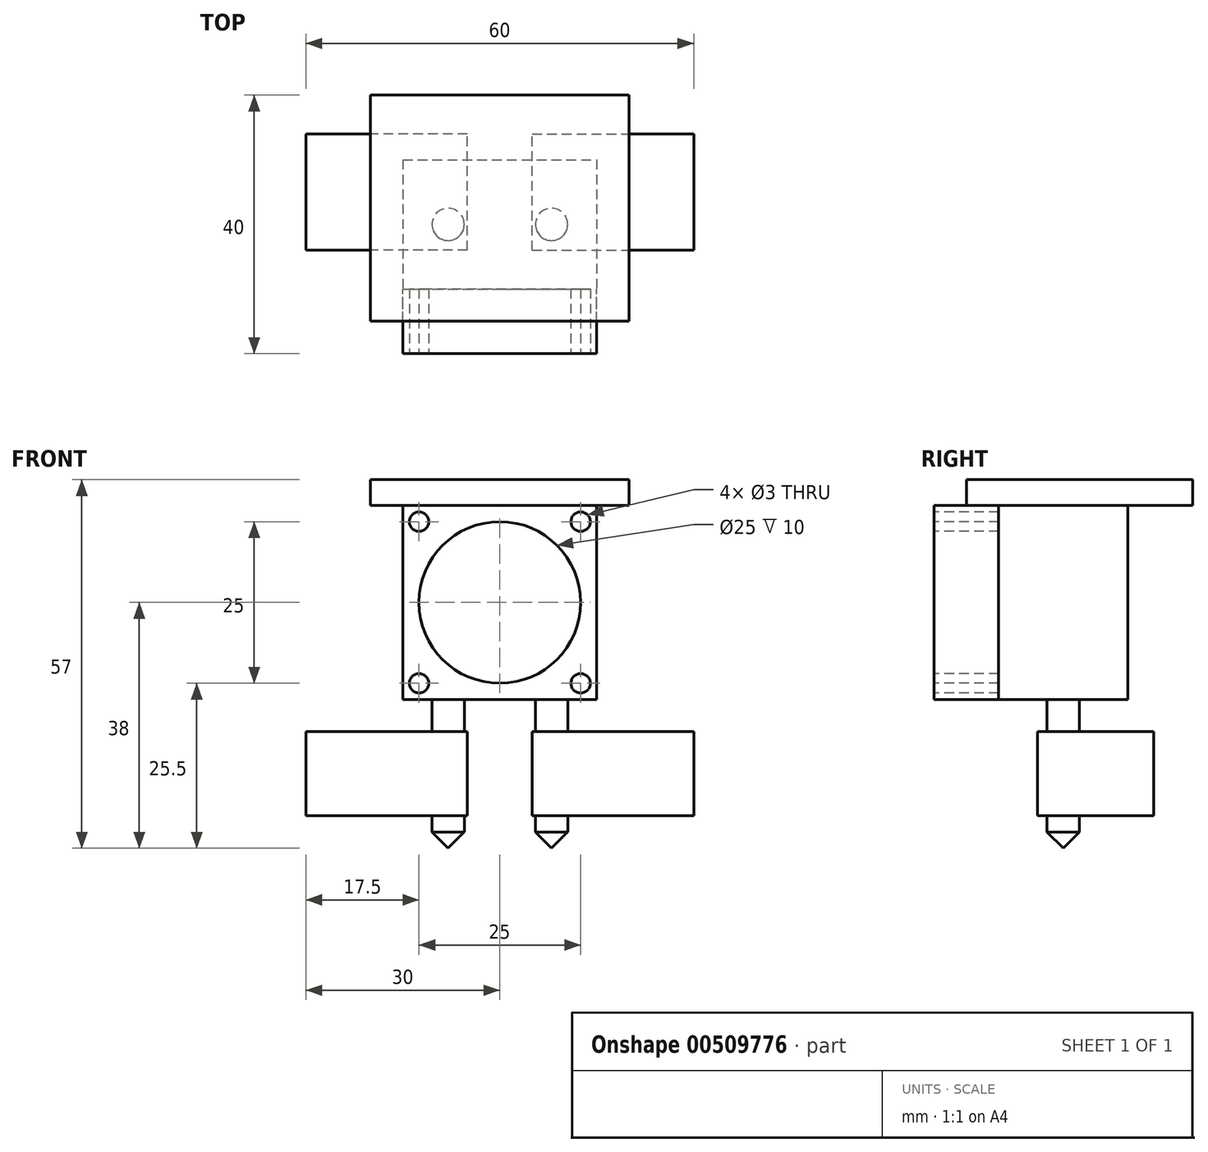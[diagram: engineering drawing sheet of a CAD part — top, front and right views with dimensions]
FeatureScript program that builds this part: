
annotation { "Feature Type Name" : "Feature", "Feature Type Description" : "" }
export const myFeature = defineFeature(function(context is Context, id is Id, definition is map)
    precondition{}
    {
        {
            var Q0;
            Q0=qCreatedBy(makeId("Top.planeOp"),FACE);
            var sketch = newSketch(context, id + "F0", { "sketchPlane" : qUnion([Q0])});
            skLineSegment(sketch, "E0.bottom", {"start": v(-20, 35) * mm, "end": v(20, 35) * mm});
            skLineSegment(sketch, "E0.top", {"start": v(-20, 0) * mm, "end": v(20, 0) * mm});
            skLineSegment(sketch, "E0.left", {"start": v(-20, 35) * mm, "end": v(-20, 0) * mm});
            skLineSegment(sketch, "E0.right", {"start": v(20, 35) * mm, "end": v(20, 0) * mm});
            skSolve(sketch);
        }
        {
            var Q0;
            Q0 = qSketchRegion(id + "F0", true);
            extrude(context, id + "F1", {"entities" : qUnion([Q0]), "depth" : 4 * mm});
        }
        {
            var Q0;
            Q0=makeQuery(id+"F1.opExtrude","CAP_FACE",FACE,{"disambiguationData":[OSD([sQuery(id+"F0.wireOp",EDGE,"E0.bottom"),sQuery(id+"F0.wireOp",EDGE,"E0.top"),sQuery(id+"F0.wireOp",EDGE,"E0.left"),sQuery(id+"F0.wireOp",EDGE,"E0.right")])],"isStart":true});
            var sketch = newSketch(context, id + "F2", { "sketchPlane" : qUnion([Q0])});
            skLineSegment(sketch, "E1.bottom", {"start": v(-15, -25) * mm, "end": v(15, -25) * mm});
            skLineSegment(sketch, "E1.top", {"start": v(-15, -5) * mm, "end": v(15, -5) * mm});
            skLineSegment(sketch, "E1.left", {"start": v(-15, -25) * mm, "end": v(-15, -5) * mm});
            skLineSegment(sketch, "E1.right", {"start": v(15, -25) * mm, "end": v(15, -5) * mm});
            skLineSegment(sketch, "E2", {"start": v(0, 0) * mm, "end": v(0, -5) * mm, "construction": true});
            skSolve(sketch);
        }
        {
            var Q0;
            Q0 = qSketchRegion(id + "F2", true);
            extrude(context, id + "F3", {"entities" : qUnion([Q0]), "depth" : 30 * mm});
        }
        {
            var Q0;
            Q0=makeQuery(id+"F3.opExtrude","SWEPT_FACE",FACE,{"disambiguationData":[OSD([sQuery(id+"F2.wireOp",EDGE,"E1.top")])]});
            var sketch = newSketch(context, id + "F4", { "sketchPlane" : qUnion([Q0])});
            skLineSegment(sketch, "E3.0", {"start": v(-15, -30) * mm, "end": v(-15, 0) * mm});
            skLineSegment(sketch, "E4.0", {"start": v(-15, -30) * mm, "end": v(15, -30) * mm});
            skLineSegment(sketch, "E5.0", {"start": v(15, -30) * mm, "end": v(15, 0) * mm});
            skLineSegment(sketch, "E6.0", {"start": v(-15, 0) * mm, "end": v(15, 0) * mm});
            skSolve(sketch);
        }
        {
            var Q0;
            Q0 = qSketchRegion(id + "F4", true);
            extrude(context, id + "F5", {"entities" : qUnion([Q0]), "depth" : 10 * mm});
        }
        {
            var Q0;
            Q0=makeQuery(id+"F5.opExtrude","CAP_FACE",FACE,{"disambiguationData":[OSD([sQuery(id+"F4.wireOp",EDGE,"E3.0"),sQuery(id+"F4.wireOp",EDGE,"E4.0"),sQuery(id+"F4.wireOp",EDGE,"E5.0"),sQuery(id+"F4.wireOp",EDGE,"E6.0")])],"isStart":false});
            var sketch = newSketch(context, id + "F6", { "sketchPlane" : qUnion([Q0])});
            skCircle(sketch, "E7", {"center": v(-12.5, -2.5) * mm, "radius": 1.5 * mm});
            skCircle(sketch, "E8", {"center": v(12.5, -2.5) * mm, "radius": 1.5 * mm});
            skCircle(sketch, "E9", {"center": v(-12.5, -27.5) * mm, "radius": 1.5 * mm});
            skCircle(sketch, "E10", {"center": v(12.5, -27.5) * mm, "radius": 1.5 * mm});
            skLineSegment(sketch, "E11", {"start": v(-12.5, -2.5) * mm, "end": v(0, -2.5) * mm, "construction": true});
            skLineSegment(sketch, "E12", {"start": v(0, -2.5) * mm, "end": v(12.5, -2.5) * mm, "construction": true});
            skLineSegment(sketch, "E13", {"start": v(-12.5, -2.5) * mm, "end": v(-12.5, -15) * mm, "construction": true});
            skPoint(sketch, "E13.endSnap0", {"position": v(-15, -15) * mm});
            skLineSegment(sketch, "E14", {"start": v(-12.5, -15) * mm, "end": v(-12.5, -27.5) * mm, "construction": true});
            skCircle(sketch, "E15", {"center": v(0, -15) * mm, "radius": 12.5 * mm});
            skSolve(sketch);
        }
        {
            var Q0;
            Q0=makeQuery(id+"F6.imprint","IMPRINT",FACE,{"disambiguationData":[TD([[makeQuery(id+"F6.imprint","IMPRINT",EDGE,{"derivedFrom":sQuery(id+"F6.wireOp",EDGE,"E7")}),1.0]])]});
            var Q1;
            Q1=makeQuery(id+"F6.imprint","IMPRINT",FACE,{"disambiguationData":[TD([[makeQuery(id+"F6.imprint","IMPRINT",EDGE,{"derivedFrom":sQuery(id+"F6.wireOp",EDGE,"E15")}),1.0]])]});
            var Q2;
            Q2=makeQuery(id+"F6.imprint","IMPRINT",FACE,{"disambiguationData":[TD([[makeQuery(id+"F6.imprint","IMPRINT",EDGE,{"derivedFrom":sQuery(id+"F6.wireOp",EDGE,"E8")}),1.0]])]});
            var Q3;
            Q3=makeQuery(id+"F6.imprint","IMPRINT",FACE,{"disambiguationData":[TD([[makeQuery(id+"F6.imprint","IMPRINT",EDGE,{"derivedFrom":sQuery(id+"F6.wireOp",EDGE,"E9")}),1.0]])]});
            var Q4;
            Q4=makeQuery(id+"F6.imprint","IMPRINT",FACE,{"disambiguationData":[TD([[makeQuery(id+"F6.imprint","IMPRINT",EDGE,{"derivedFrom":sQuery(id+"F6.wireOp",EDGE,"E10")}),1.0]])]});
            extrude(context, id + "F7", {"entities" : qUnion([Q0, Q1, Q2, Q3, Q4]), "operationType" : NewBodyOperationType.REMOVE, "endBound" : BoundingType.UP_TO_NEXT, "oppositeDirection" : true, "depth" : 25 * mm});
        }
        {
            var Q0;
            Q0=makeQuery(id+"F3.opExtrude","CAP_FACE",FACE,{"disambiguationData":[OSD([sQuery(id+"F2.wireOp",EDGE,"E1.bottom"),sQuery(id+"F2.wireOp",EDGE,"E1.top"),sQuery(id+"F2.wireOp",EDGE,"E1.left"),sQuery(id+"F2.wireOp",EDGE,"E1.right")])],"isStart":false});
            var sketch = newSketch(context, id + "F8", { "sketchPlane" : qUnion([Q0])});
            skCircle(sketch, "E16", {"center": v(-8, -15) * mm, "radius": 2.5 * mm});
            skPoint(sketch, "E16.centerSnap0", {"position": v(-15, -15) * mm});
            skCircle(sketch, "E17", {"center": v(8, -15) * mm, "radius": 2.5 * mm});
            skPoint(sketch, "E17.centerSnap0", {"position": v(15, -15) * mm});
            skLineSegment(sketch, "E18", {"start": v(-8, -15) * mm, "end": v(0, -15) * mm, "construction": true});
            skLineSegment(sketch, "E19", {"start": v(0, -15) * mm, "end": v(8, -15) * mm, "construction": true});
            skSolve(sketch);
        }
        {
            var Q0;
            Q0 = qSketchRegion(id + "F8", true);
            extrude(context, id + "F9", {"entities" : qUnion([Q0]), "operationType" : NewBodyOperationType.ADD, "depth" : 5 * mm});
        }
        {
            var Q0;
            Q0=makeQuery(id+"F9.opExtrude","CAP_FACE",FACE,{"disambiguationData":[OSD([sQuery(id+"F8.wireOp",EDGE,"E17")])],"isStart":false});
            var sketch = newSketch(context, id + "F10", { "sketchPlane" : qUnion([Q0])});
            skLineSegment(sketch, "E20.bottom", {"start": v(5, -11) * mm, "end": v(30, -11) * mm});
            skLineSegment(sketch, "E20.top", {"start": v(5, -29) * mm, "end": v(30, -29) * mm});
            skLineSegment(sketch, "E20.left", {"start": v(5, -11) * mm, "end": v(5, -29) * mm});
            skLineSegment(sketch, "E20.right", {"start": v(30, -11) * mm, "end": v(30, -29) * mm});
            skLineSegment(sketch, "E21.MirrorCS", {"start": v(-5, -11) * mm, "end": v(-5, -29) * mm});
            skLineSegment(sketch, "E22.MirrorCS", {"start": v(-5, -11) * mm, "end": v(-30, -11) * mm});
            skLineSegment(sketch, "E23.MirrorCS", {"start": v(-30, -11) * mm, "end": v(-30, -29) * mm});
            skLineSegment(sketch, "E24.MirrorCS", {"start": v(-5, -29) * mm, "end": v(-30, -29) * mm});
            skSolve(sketch);
        }
        {
            var Q0;
            Q0 = qSketchRegion(id + "F10", true);
            extrude(context, id + "F11", {"entities" : qUnion([Q0]), "operationType" : NewBodyOperationType.ADD, "depth" : 13 * mm});
        }
        {
            var Q0;
            Q0=makeQuery(id+"F11.opExtrude","CAP_FACE",FACE,{"disambiguationData":[OSD([sQuery(id+"F10.wireOp",EDGE,"E20.bottom"),sQuery(id+"F10.wireOp",EDGE,"E20.top"),sQuery(id+"F10.wireOp",EDGE,"E20.left"),sQuery(id+"F10.wireOp",EDGE,"E20.right")])],"isStart":false});
            var sketch = newSketch(context, id + "F12", { "sketchPlane" : qUnion([Q0])});
            skCircle(sketch, "E25.0", {"center": v(8, -15) * mm, "radius": 2.5 * mm});
            skCircle(sketch, "E26.0", {"center": v(-8, -15) * mm, "radius": 2.5 * mm});
            skSolve(sketch);
        }
        {
            var Q0;
            Q0 = qSketchRegion(id + "F12", true);
            extrude(context, id + "F13", {"entities" : qUnion([Q0]), "operationType" : NewBodyOperationType.ADD, "depth" : 5 * mm});
        }
        {
            var Q0;
            Q0=makeQuery(id+"F13.opExtrude","CAP_EDGE",EDGE,{"disambiguationData":[OSD([sQuery(id+"F12.wireOp",EDGE,"E26.0")])],"isStart":false});
            var Q1;
            Q1=makeQuery(id+"F13.opExtrude","CAP_EDGE",EDGE,{"disambiguationData":[OSD([sQuery(id+"F12.wireOp",EDGE,"E25.0")])],"isStart":false});
            chamfer(context, id + "F14", {"entities" : qUnion([Q0, Q1]), "width" : 2.5 * mm, "tangentPropagation" : true});
        }
    });
